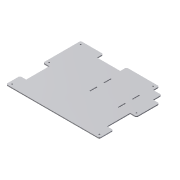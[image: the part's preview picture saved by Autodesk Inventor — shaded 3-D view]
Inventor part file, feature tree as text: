
AUTODESK INVENTOR PART (.ipt)
format: ipt  version: 2014 (Build 180170000, 170)  size: 227,840 bytes
history: native  units: mm
features: extrude x5, sketch x5, fillet x1
ambient origin geometry x8: Origin, YZ Plane, XZ Plane, XY Plane, X Axis, Y Axis, Z Axis, Center Point
bodies: Solid1 (feature_tree)
feature tree (11):
  extrude  "Extrusion1"  Depth=300.0mm
  extrude  "Extrusion6"  Depth=25.0mm
  extrude  "Extrusion7"  Depth=4.0mm
  extrude  "Extrusion8"  Depth=4.0mm TaperAngle=0.0deg
  extrude  "Extrusion9"  Depth=34.0mm
  fillet  "Fillet3"  Radius=12.5mm
  sketch  "Sketch1"  dims[d0=375.0mm d1=300.0mm]
  sketch  "Sketch6"  dims[d2=4.0mm d3=0.0mm d22=25.0mm]
  sketch  "Sketch7"  dims[d23=4.0mm d24=0.0mm d25=160.0mm]
  sketch  "Sketch8"  dims[d26=200.0mm d28=4.0mm d29=0.0mm]
  sketch  "Sketch9"  dims[d30=6.0mm d31=34.0mm d32=12.5mm d33=12.5mm d34=12.5mm d35=12.5mm d36=12.5mm d37=5.4mm d38=10.0mm d39=0.0mm d40=114.0mm d41=2.15mm d42=56.6mm d43=25.0mm d44=85.0mm d45=10.0mm d46=0.0mm]
